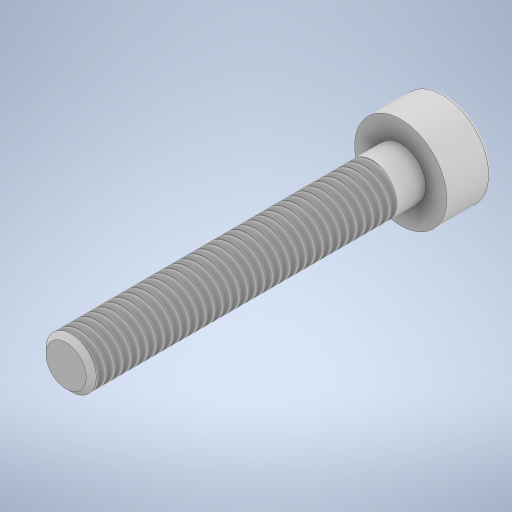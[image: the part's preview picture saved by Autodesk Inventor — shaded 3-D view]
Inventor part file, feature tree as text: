
AUTODESK INVENTOR PART (.ipt)
format: ipt  version: 2024 (Build 280153000, 153)  size: 302,592 bytes
history: native  units: in
note: dims shown in document units (in); Inventor stores cm internally (conversion verified against a paired STEP export)
features: extrude x3, sketch x2, plane x1, chamfer x1, thread x1, fillet x1
ambient origin geometry x8: Origin, YZ Plane, XZ Plane, XY Plane, X Axis, Y Axis, Z Axis, Center Point
bodies: Solid1 (feature_tree)
feature tree (9):
  sketch  "Sketch1"  dims[d0=0.2165in d1=0.1137in]
  extrude  "Extrusion1"  Depth=0.1137in
  extrude  "Extrusion2"  Depth=0.0492in TaperAngle=0.0deg
  plane  "Work Plane1"
  extrude  "Extrusion3"  TaperAngle=0.0deg  [1 undecoded]
  chamfer  "Chamfer1"  Distance=0.1181in
  thread  "Thread1"  [1 undecoded]
  fillet  "Fillet1"  Radius=0.0118in
  sketch  "Sketch2"  dims[d2=0.1063in d3=0.0in d4=0.0492in d5=0.0in d6=0.0in d7=0.1181in d8=0.7874in d9=0.0in d10=0.0118in d11=0.0787in d12=45.0deg d13=0.7087in d14=0.0in d15=0.0079in]
note: 2 required parameter values undecoded (feature->parameter linkage not recoverable at this tier; creation-order binding heuristic only, values carry confidence <= 0.55)
